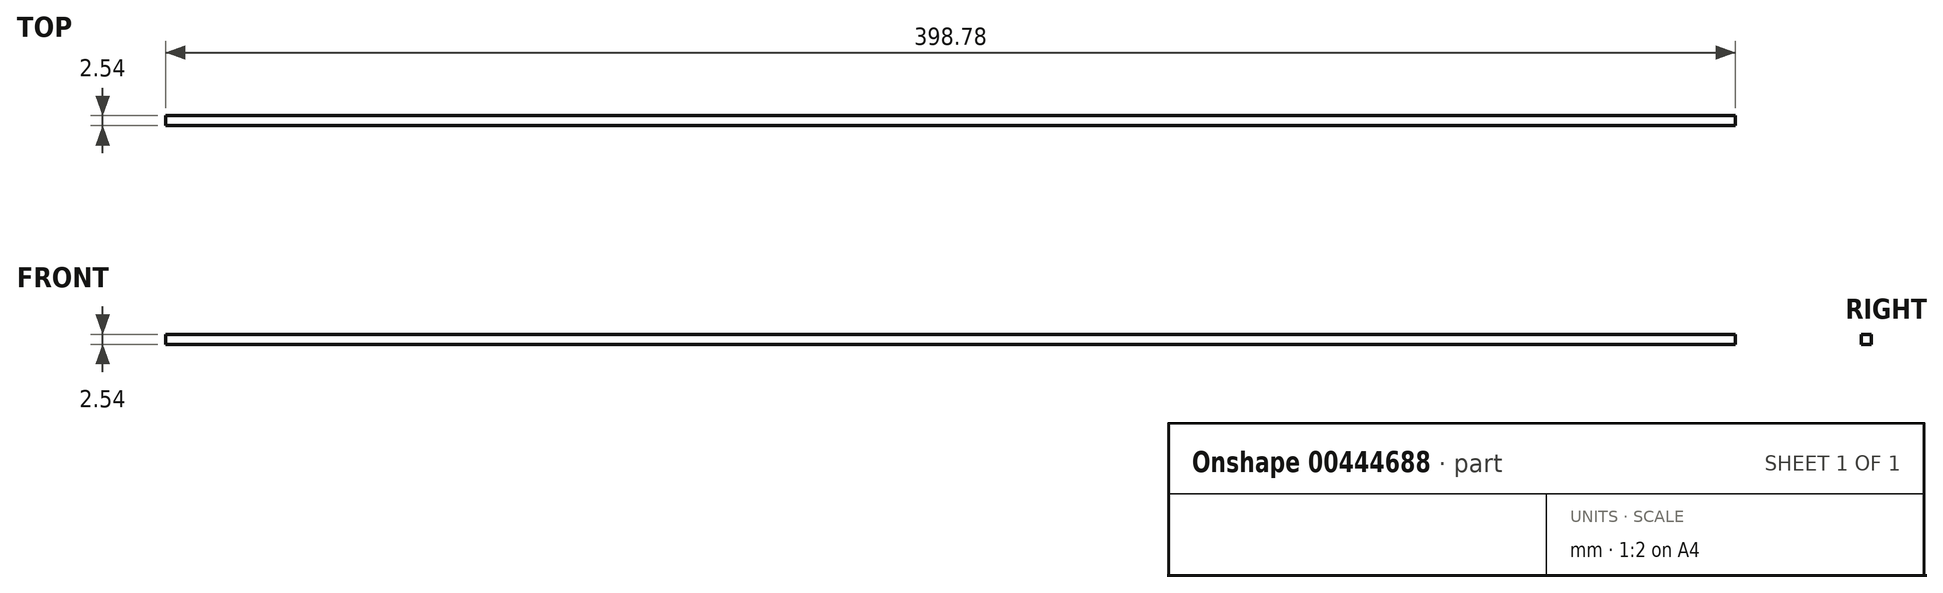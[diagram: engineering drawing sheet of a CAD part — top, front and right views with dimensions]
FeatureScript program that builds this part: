
annotation { "Feature Type Name" : "Feature", "Feature Type Description" : "" }
export const myFeature = defineFeature(function(context is Context, id is Id, definition is map)
    precondition{}
    {
        {
            var Q0;
            Q0=qCreatedBy(makeId("Top.planeOp"),FACE);
            var sketch = newSketch(context, id + "F0", { "sketchPlane" : qUnion([Q0])});
            skLineSegment(sketch, "E0.bottom", {"start": v(-199.08, 5.06) * mm, "end": v(199.7, 5.06) * mm});
            skLineSegment(sketch, "E0.top", {"start": v(-199.08, 2.52) * mm, "end": v(199.7, 2.52) * mm});
            skLineSegment(sketch, "E0.left", {"start": v(-199.08, 5.06) * mm, "end": v(-199.08, 2.52) * mm});
            skLineSegment(sketch, "E0.right", {"start": v(199.7, 5.06) * mm, "end": v(199.7, 2.52) * mm});
            skSolve(sketch);
        }
        {
            var Q0;
            Q0 = qSketchRegion(id + "F0", true);
            extrude(context, id + "F1", {"entities" : qUnion([Q0]), "depth" : 2.54 * mm});
        }
    });
